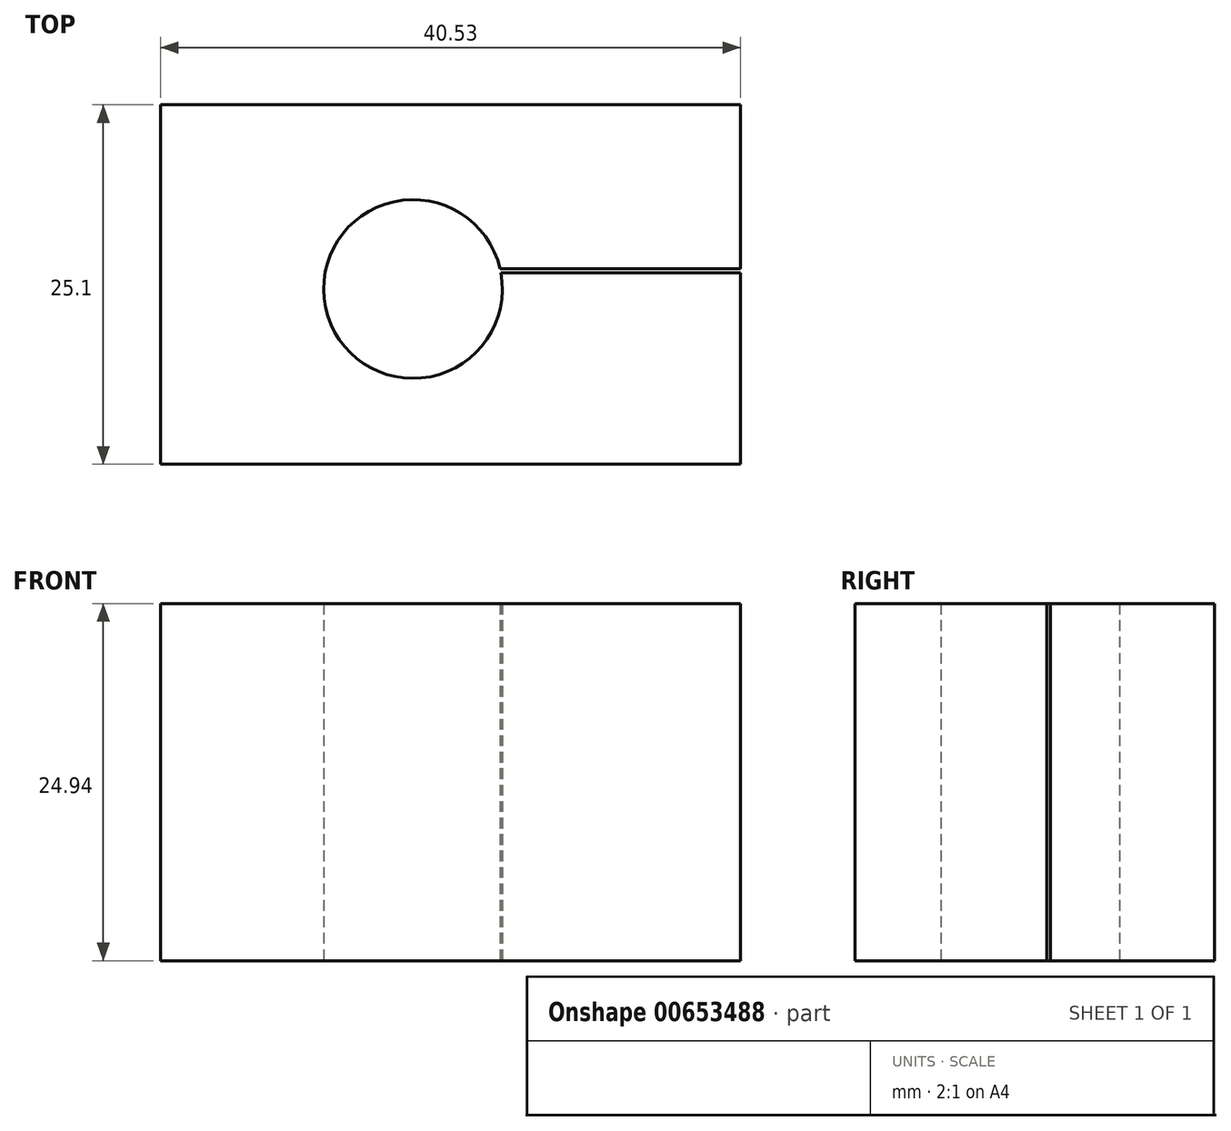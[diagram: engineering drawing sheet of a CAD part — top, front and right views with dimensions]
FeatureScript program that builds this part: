
annotation { "Feature Type Name" : "Feature", "Feature Type Description" : "" }
export const myFeature = defineFeature(function(context is Context, id is Id, definition is map)
    precondition{}
    {
        {
            var Q0;
            Q0=qCreatedBy(makeId("Top.planeOp"),FACE);
            var sketch = newSketch(context, id + "F0", { "sketchPlane" : qUnion([Q0])});
            skLineSegment(sketch, "E0", {"start": v(-16.06, 17.57) * mm, "end": v(24.47, 17.57) * mm});
            skLineSegment(sketch, "E1", {"start": v(24.47, 17.57) * mm, "end": v(24.47, 6.12) * mm});
            skLineSegment(sketch, "E2", {"start": v(-16.06, 17.57) * mm, "end": v(-16.06, -7.53) * mm});
            skLineSegment(sketch, "E3", {"start": v(24.47, -7.53) * mm, "end": v(-16.06, -7.53) * mm});
            skArc(sketch, "E4", {"start": v(7.67, 6.12) * mm, "mid": v(-4.53, 3.43) * mm, "end": v(7.72, 5.85) * mm});
            skLineSegment(sketch, "E5", {"start": v(24.47, 6.12) * mm, "end": v(7.67, 6.12) * mm});
            skLineSegment(sketch, "E6", {"start": v(24.47, 5.85) * mm, "end": v(7.72, 5.85) * mm});
            skLineSegment(sketch, "E7", {"start": v(24.47, 5.85) * mm, "end": v(24.47, -7.53) * mm});
            skSolve(sketch);
        }
        {
            var Q0;
            Q0=makeQuery(id+"F0.imprint","IMPRINT",FACE,{"disambiguationData":[TD([[makeQuery(id+"F0.imprint","IMPRINT",EDGE,{"derivedFrom":sQuery(id+"F0.wireOp",EDGE,"E0")}),-1.0]])]});
            extrude(context, id + "F1", {"entities" : qUnion([Q0]), "depth" : 24.94 * mm, "offsetDistance" : 25 * mm});
        }
    });
